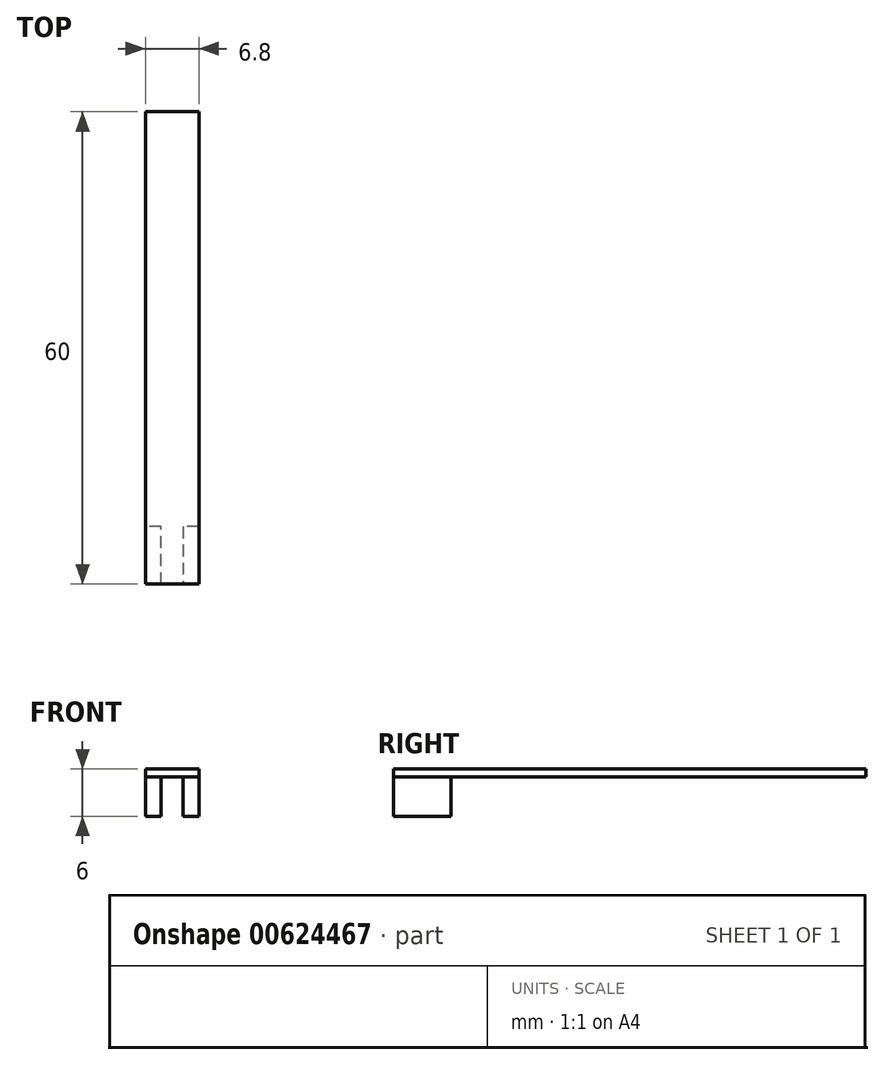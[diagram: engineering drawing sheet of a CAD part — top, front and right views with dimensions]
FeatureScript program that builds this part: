
annotation { "Feature Type Name" : "Feature", "Feature Type Description" : "" }
export const myFeature = defineFeature(function(context is Context, id is Id, definition is map)
    precondition{}
    {
        {
            var Q0;
            Q0=qCreatedBy(makeId("Top.planeOp"),FACE);
            var sketch = newSketch(context, id + "F0", { "sketchPlane" : qUnion([Q0])});
            skLineSegment(sketch, "E0", {"start": v(-1.4, 0) * mm, "end": v(-1.4, 7.3) * mm});
            skLineSegment(sketch, "E1", {"start": v(-1.4, 7.3) * mm, "end": v(-3.4, 7.3) * mm});
            skLineSegment(sketch, "E2", {"start": v(-3.4, 7.3) * mm, "end": v(-3.4, 0) * mm});
            skLineSegment(sketch, "E3", {"start": v(-3.4, 0) * mm, "end": v(3.4, 0) * mm});
            skLineSegment(sketch, "E4", {"start": v(3.4, 0) * mm, "end": v(3.4, 7.3) * mm});
            skLineSegment(sketch, "E5", {"start": v(3.4, 7.3) * mm, "end": v(1.4, 7.3) * mm});
            skLineSegment(sketch, "E6", {"start": v(1.4, 7.3) * mm, "end": v(1.4, 0) * mm});
            skSolve(sketch);
        }
        {
            var Q0;
            Q0 = qSketchRegion(id + "F0", true);
            extrude(context, id + "F1", {"entities" : qUnion([Q0]), "depth" : 5 * mm, "offsetDistance" : 25 * mm});
        }
        {
            var Q0;
            Q0=makeQuery(id+"F1.opExtrude","CAP_FACE",FACE,{"disambiguationData":[OSD([sQuery(id+"F0.wireOp",EDGE,"E3"),sQuery(id+"F0.wireOp",EDGE,"E4"),sQuery(id+"F0.wireOp",EDGE,"E5"),sQuery(id+"F0.wireOp",EDGE,"E6")])],"isStart":false});
            var sketch = newSketch(context, id + "F2", { "sketchPlane" : qUnion([Q0])});
            skLineSegment(sketch, "E7.bottom", {"start": v(3.4, 0) * mm, "end": v(-3.4, 0) * mm});
            skLineSegment(sketch, "E7.top", {"start": v(3.4, 60) * mm, "end": v(-3.4, 60) * mm});
            skLineSegment(sketch, "E7.left", {"start": v(3.4, 0) * mm, "end": v(3.4, 60) * mm});
            skLineSegment(sketch, "E7.right", {"start": v(-3.4, 0) * mm, "end": v(-3.4, 60) * mm});
            skSolve(sketch);
        }
        {
            var Q0;
            Q0 = qSketchRegion(id + "F2", true);
            extrude(context, id + "F3", {"entities" : qUnion([Q0]), "depth" : 1 * mm, "offsetDistance" : 25 * mm});
        }
    });
